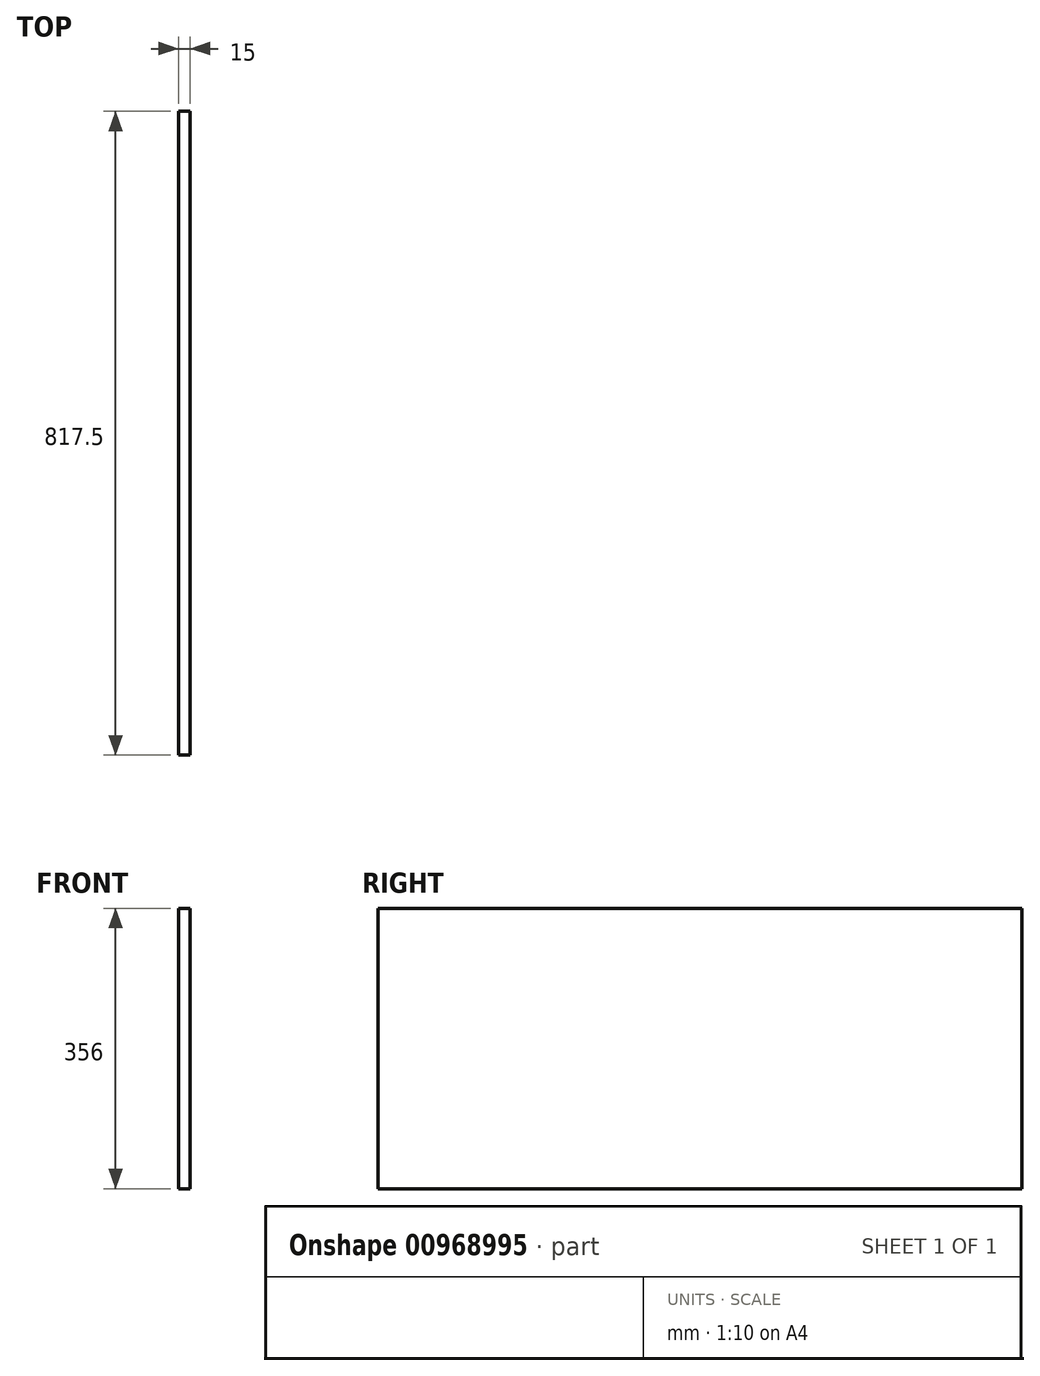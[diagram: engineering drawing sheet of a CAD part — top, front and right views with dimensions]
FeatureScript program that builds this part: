
annotation { "Feature Type Name" : "Feature", "Feature Type Description" : "" }
export const myFeature = defineFeature(function(context is Context, id is Id, definition is map)
    precondition{}
    {
        {
            var Q0;
            Q0=qCreatedBy(makeId("Front.planeOp"),FACE);
            var sketch = newSketch(context, id + "F0", { "sketchPlane" : qUnion([Q0])});
            skLineSegment(sketch, "E0.bottom", {"start": v(7.5, 178) * mm, "end": v(-7.5, 178) * mm});
            skLineSegment(sketch, "E0.top", {"start": v(7.5, -178) * mm, "end": v(-7.5, -178) * mm});
            skLineSegment(sketch, "E0.left", {"start": v(7.5, 178) * mm, "end": v(7.5, -178) * mm});
            skLineSegment(sketch, "E0.right", {"start": v(-7.5, 178) * mm, "end": v(-7.5, -178) * mm});
            skPoint(sketch, "E0.middle", {"position": v(0, 0) * mm});
            skSolve(sketch);
        }
        {
            var Q0;
            Q0=makeQuery(id+"F0.imprint","IMPRINT",FACE,{"disambiguationData":[TD([[makeQuery(id+"F0.imprint","IMPRINT",EDGE,{"derivedFrom":sQuery(id+"F0.wireOp",EDGE,"E0.bottom")}),1.0]])]});
            extrude(context, id + "F1", {"entities" : qUnion([Q0]), "depth" : ((1000 - 90 - 90) - 2.5) * mm, "offsetDistance" : 25 * mm});
        }
    });
